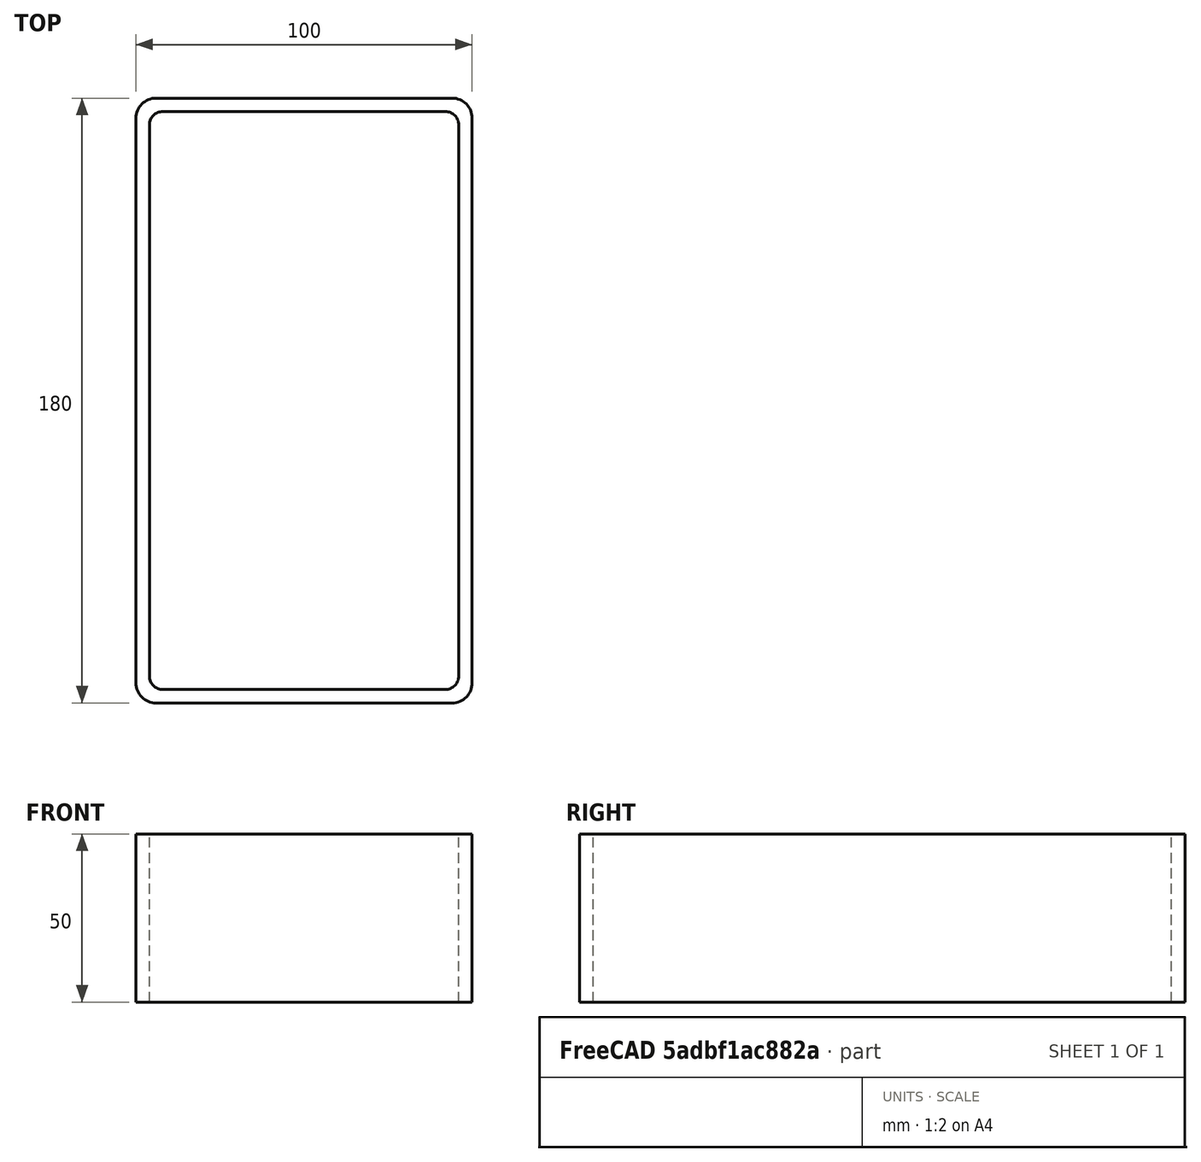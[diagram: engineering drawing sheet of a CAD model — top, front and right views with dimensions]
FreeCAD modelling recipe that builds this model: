
FCSTD DOCUMENT  (FreeCAD 0.15R4671 (Git))
Label: Rectangular hollow section 180x100x4 EN10219 S235JRH
License: All rights reserved
LicenseURL: http://en.wikipedia.org/wiki/All_rights_reserved
objects: Sketcher::SketchObject×1, Part::Extrusion×1
note: 2 computed .brp shape members not serialized (recipe doc carries the construction recipe); baked Part::Feature solids carry a one-line shape summary decoded from their .brp

FEATURE [Sketcher::SketchObject] Sketch
  sketch-geometry (16):
    g0: LineSegment StartX=-42 StartY=86 StartZ=0 EndX=42 EndY=86 EndZ=0
    g1: LineSegment StartX=46 StartY=82 StartZ=0 EndX=46 EndY=-82 EndZ=0
    g2: LineSegment StartX=42 StartY=-86 StartZ=0 EndX=-42 EndY=-86 EndZ=0
    g3: LineSegment StartX=-46 StartY=-82 StartZ=0 EndX=-46 EndY=82 EndZ=0
    g4: LineSegment StartX=-44 StartY=90 StartZ=0 EndX=44 EndY=90 EndZ=0
    g5: LineSegment StartX=50 StartY=84 StartZ=0 EndX=50 EndY=-84 EndZ=0
    g6: LineSegment StartX=44 StartY=-90 StartZ=0 EndX=-44 EndY=-90 EndZ=0
    g7: LineSegment StartX=-50 StartY=-84 StartZ=0 EndX=-50 EndY=84 EndZ=0
    g8: ArcOfCircle CenterX=-42 CenterY=82 CenterZ=0 NormalX=0 NormalY=0 NormalZ=1 Radius=4 StartAngle=1.5708 EndAngle=3.14159
    g9: ArcOfCircle CenterX=42 CenterY=82 CenterZ=0 NormalX=0 NormalY=0 NormalZ=1 Radius=4 StartAngle=0 EndAngle=1.5708
    g10: ArcOfCircle CenterX=42 CenterY=-82 CenterZ=0 NormalX=0 NormalY=0 NormalZ=1 Radius=4 StartAngle=4.71239 EndAngle=6.28319
    g11: ArcOfCircle CenterX=-42 CenterY=-82 CenterZ=0 NormalX=0 NormalY=0 NormalZ=1 Radius=4 StartAngle=3.14159 EndAngle=4.71239
    g12: ArcOfCircle CenterX=44 CenterY=84 CenterZ=0 NormalX=0 NormalY=0 NormalZ=1 Radius=6 StartAngle=0 EndAngle=1.5708
    g13: ArcOfCircle CenterX=44 CenterY=-84 CenterZ=0 NormalX=0 NormalY=0 NormalZ=1 Radius=6 StartAngle=4.71239 EndAngle=6.28319
    g14: ArcOfCircle CenterX=-44 CenterY=-84 CenterZ=0 NormalX=0 NormalY=0 NormalZ=1 Radius=6 StartAngle=3.14159 EndAngle=4.71239
    g15: ArcOfCircle CenterX=-44 CenterY=84 CenterZ=0 NormalX=0 NormalY=0 NormalZ=1 Radius=6 StartAngle=1.5708 EndAngle=3.14159
  constraints (36):
    c: Horizontal(g2)
    c: Vertical(g3)
    c: Horizontal(g6)
    c: Vertical(g7)
    c: Tangent(g3,g8) = 1.5708
    c: Tangent(g0,g8) = 1.5708
    c: Tangent(g0,g9) = 1.5708
    c: Tangent(g1,g9) = 1.5708
    c: Tangent(g1,g10) = 1.5708
    c: Tangent(g2,g10) = 1.5708
    c: Tangent(g2,g11) = 1.5708
    c: Tangent(g3,g11) = 1.5708
    c: Tangent(g4,g12) = 1.5708
    c: Tangent(g5,g12) = 1.5708
    c: Tangent(g5,g13) = 1.5708
    c: Tangent(g6,g13) = 1.5708
    c: Tangent(g6,g14) = 1.5708
    c: Tangent(g7,g14) = 1.5708
    c: Tangent(g7,g15) = 1.5708
    c: Tangent(g4,g15) = 1.5708
    c: Equal(g9,g8)
    c: Equal(g9,g11)
    c: Equal(g9,g10)
    c: Equal(g12,g15)
    c: Equal(g12,g14)
    c: Equal(g12,g13)
    c: Symmetric(g4,g6,g-1)
    c: Symmetric(g7,g5,g-2)
    c: DistanceY(g4,g6) = -180
    c: DistanceX(g7,g5) = 100
    c: Symmetric(g3,g1,g-2)
    c: Symmetric(g0,g2,g-1)
    c: DistanceY(g0,g4) = 4
    c: DistanceX(g5,g1) = -4
    c: Radius(g9) = 4
    c: Radius(g12) = 6
FEATURE [Part::Extrusion] Extrude  label="Rectangular hollow section 180x100x4 EN10219 S235JRH"
  Base = -> Sketch
  Dir = (0,0,50)
  Solid = true
